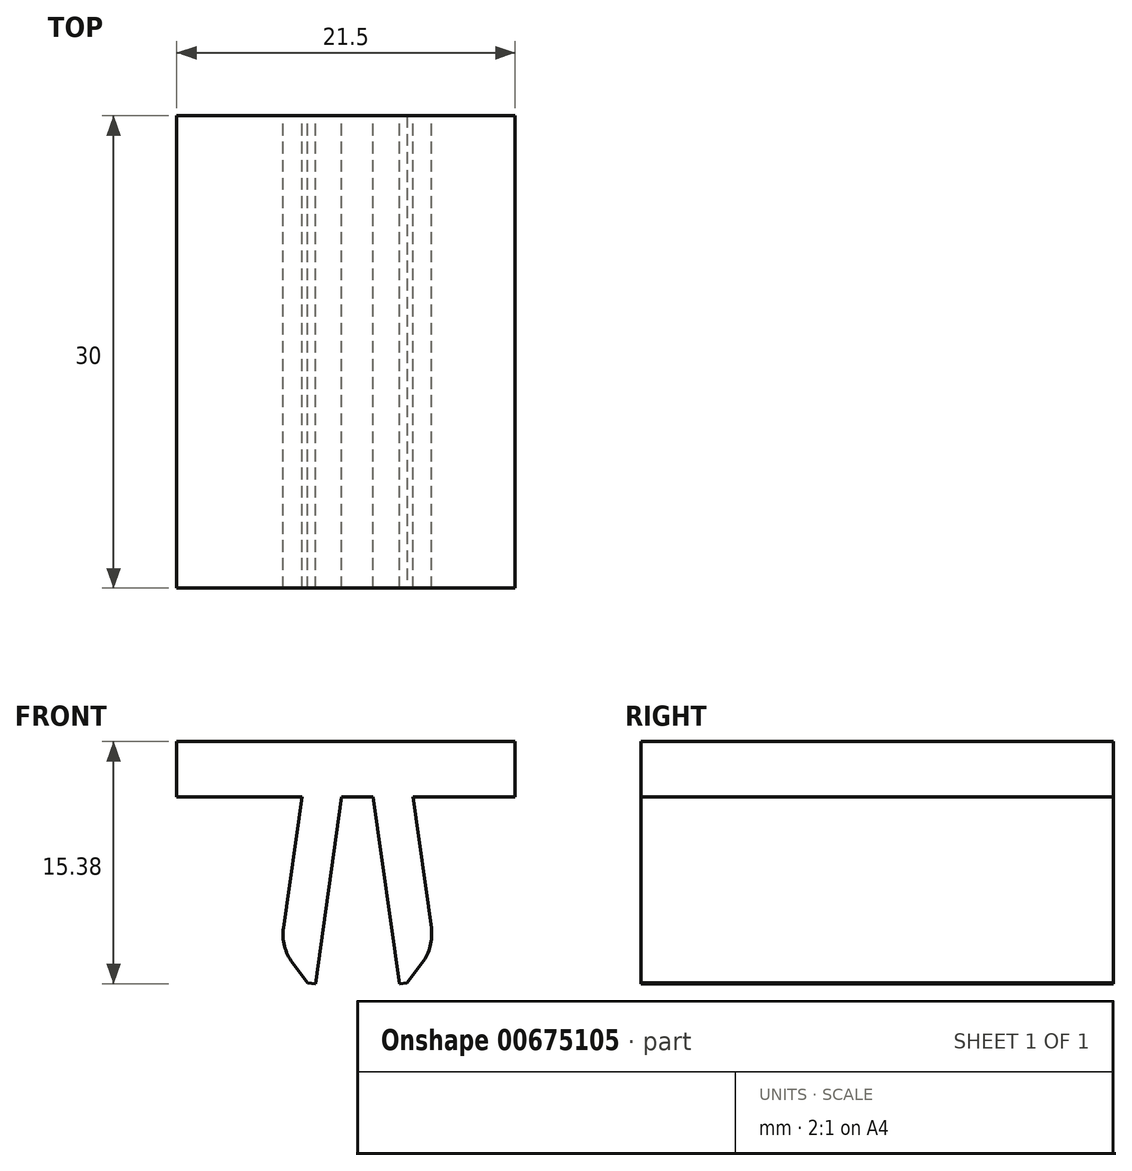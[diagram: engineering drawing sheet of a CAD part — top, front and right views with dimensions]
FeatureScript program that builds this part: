
annotation { "Feature Type Name" : "Feature", "Feature Type Description" : "" }
export const myFeature = defineFeature(function(context is Context, id is Id, definition is map)
    precondition{}
    {
        {
            var Q0;
            Q0=qCreatedBy(makeId("Front.planeOp"),FACE);
            var sketch = newSketch(context, id + "F0", { "sketchPlane" : qUnion([Q0])});
            skLineSegment(sketch, "E0.bottom", {"start": v(0, 0) * mm, "end": v(20, 0) * mm});
            skLineSegment(sketch, "E0.top", {"start": v(0, 3.5) * mm, "end": v(20, 3.5) * mm});
            skLineSegment(sketch, "E0.left", {"start": v(0, 0) * mm, "end": v(0, 3.5) * mm});
            skLineSegment(sketch, "E0.right", {"start": v(20, 0) * mm, "end": v(20, 3.5) * mm});
            skLineSegment(sketch, "E1", {"start": v(10, 0) * mm, "end": v(11.62, -11.54) * mm});
            skLineSegment(sketch, "E2", {"start": v(11.62, -11.54) * mm, "end": v(11.62, -11.54) * mm});
            skLineSegment(sketch, "E3", {"start": v(7.48, 0) * mm, "end": v(9.15, -11.88) * mm});
            skLineSegment(sketch, "E4", {"start": v(9.15, -11.88) * mm, "end": v(11.62, -11.54) * mm});
            skLineSegment(sketch, "E5", {"start": v(5.48, 0) * mm, "end": v(3.8, -11.88) * mm});
            skLineSegment(sketch, "E6", {"start": v(3.8, -11.88) * mm, "end": v(1.33, -11.54) * mm});
            skLineSegment(sketch, "E7", {"start": v(1.33, -11.54) * mm, "end": v(2.95, 0) * mm});
            skLineSegment(sketch, "E8", {"start": v(2.95, 0) * mm, "end": v(5.48, 0) * mm});
            skLineSegment(sketch, "E9.bottom", {"start": v(12.5, 0) * mm, "end": v(15.5, 0) * mm});
            skSolve(sketch);
        }
        {
            var Q0;
            Q0=makeQuery(id+"F0.imprint","IMPRINT",FACE,{"disambiguationData":[TD([[makeQuery(id+"F0.imprint","IMPRINT",EDGE,{"derivedFrom":sQuery(id+"F0.wireOp",EDGE,"E5")}),-1.0]])]});
            var Q1;
            {var subQ6=sQuery(id+"F0.wireOp",EDGE,"E3");Q1=makeQuery(id+"F0.imprint","IMPRINT",FACE,{"disambiguationData":[TD([[makeQuery(id+"F0.imprint","IMPRINT",EDGE,{"derivedFrom":subQ6}),1.0]])]});}
            var Q2;
            {var subQ0=sQuery(id+"F0.wireOp",EDGE,"2e35a05b-6540-4c61-9137-7174225991f0");Q2=makeQuery(id+"F0.imprint","IMPRINT",FACE,{"disambiguationData":[TD([[makeQuery(id+"F0.imprint","IMPRINT",EDGE,{"derivedFrom":subQ0}),1.0]])]});}
            var Q3;
            {var subQ0=sQuery(id+"F0.wireOp",EDGE,"a4403f19-2164-46cf-9fac-c199856bc08c");Q3=makeQuery(id+"F0.imprint","IMPRINT",FACE,{"disambiguationData":[TD([[makeQuery(id+"F0.imprint","IMPRINT",EDGE,{"derivedFrom":subQ0}),1.0]])]});}
            var Q4;
            Q4=makeQuery(id+"F0.imprint","IMPRINT",FACE,{"disambiguationData":[TD([[makeQuery(id+"F0.imprint","IMPRINT",EDGE,{"derivedFrom":sQuery(id+"F0.wireOp",EDGE,"E0.top")}),-1.0]])]});
            extrude(context, id + "F1", {"entities" : qUnion([Q0, Q1, Q2, Q3, Q4]), "depth" : 30 * mm, "offsetDistance" : 25 * mm});
        }
        {
            var Q0;
            Q0=makeQuery(id+"F1.opExtrude","SWEPT_FACE",FACE,{"disambiguationData":[OSD([sQuery(id+"F0.wireOp",EDGE,"E0.right")])]});
            extrude(context, id + "F2", {"entities" : qUnion([Q0]), "operationType" : NewBodyOperationType.REMOVE, "oppositeDirection" : true, "depth" : 3.5 * mm, "offsetDistance" : 25 * mm});
        }
        {
            var Q0;
            Q0=makeQuery(id+"F1.opExtrude","SWEPT_FACE",FACE,{"disambiguationData":[OSD([sQuery(id+"F0.wireOp",EDGE,"E0.left")])]});
            extrude(context, id + "F3", {"entities" : qUnion([Q0]), "operationType" : NewBodyOperationType.ADD, "depth" : 5 * mm, "offsetDistance" : 25 * mm});
        }
        {
            var Q0;
            Q0=makeQuery(id+"F1.opExtrude","SWEPT_EDGE",EDGE,{"disambiguationData":[OSD([sQuery(id+"F0.wireOp",EDGE,"E1"),sQuery(id+"F0.wireOp",EDGE,"E4")])]});
            var Q1;
            Q1=makeQuery(id+"F1.opExtrude","SWEPT_EDGE",EDGE,{"disambiguationData":[OSD([sQuery(id+"F0.wireOp",EDGE,"E6"),sQuery(id+"F0.wireOp",EDGE,"E7")])]});
            chamfer(context, id + "F4", {"entities" : qUnion([Q0, Q1]), "width" : 2 * mm, "tangentPropagation" : true});
        }
        {
            var Q0;
            {var subQ0=sQuery(id+"F0.wireOp",EDGE,"E7");Q0=makeQuery(id+"F4.opChamfer","BLEND_EDGE",EDGE,{"blendedFrom":[makeQuery(id+"F1.opExtrude","SWEPT_EDGE",EDGE,{"disambiguationData":[OSD([sQuery(id+"F0.wireOp",EDGE,"E6"),subQ0])]}),makeQuery(id+"F1.opExtrude","SWEPT_FACE",FACE,{"disambiguationData":[OSD([subQ0])]})],"blendedInto":[makeQuery(id+"F1.opExtrude","SWEPT_FACE",FACE,{"disambiguationData":[OSD([subQ0])]})]});}
            var Q1;
            {var subQ0=sQuery(id+"F0.wireOp",EDGE,"E1");Q1=makeQuery(id+"F4.opChamfer","BLEND_EDGE",EDGE,{"blendedFrom":[makeQuery(id+"F1.opExtrude","SWEPT_EDGE",EDGE,{"disambiguationData":[OSD([subQ0,sQuery(id+"F0.wireOp",EDGE,"E4")])]}),makeQuery(id+"F1.opExtrude","SWEPT_FACE",FACE,{"disambiguationData":[OSD([subQ0])]})],"blendedInto":[makeQuery(id+"F1.opExtrude","SWEPT_FACE",FACE,{"disambiguationData":[OSD([subQ0])]})]});}
            fillet(context, id + "F5", {"entities" : qUnion([Q0, Q1]), "radius" : 3 * mm, "tangentPropagation" : true, "allowEdgeOverflow" : false});
        }
    });
